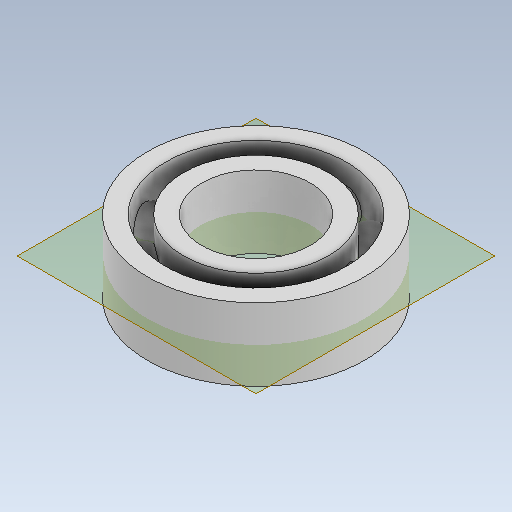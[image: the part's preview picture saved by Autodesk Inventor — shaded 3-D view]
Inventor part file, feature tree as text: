
AUTODESK INVENTOR PART (.ipt)
format: ipt  version: 2020 (Build 240168000, 168)  size: 228,864 bytes
history: native  units: mm
features: sketch x3, extrude x2, plane x1, revolve x1, pattern_circular x1, projected_geometry x1
ambient origin geometry x8: Origin, YZ Plane, XZ Plane, XY Plane, X Axis, Y Axis, Z Axis, Center Point
bodies: Solid1 (feature_tree)
feature tree (9):
  extrude  "Extrusion1"  Depth=3.0mm
  extrude  "Extrusion2"  Depth=4.0mm
  plane  "Work Plane1"
  revolve  "Revolution1"  [1 undecoded]
  pattern_circular  "Circular Pattern1"  [2 undecoded]
  sketch  "Sketch1"  dims[d0=6.0mm d1=3.0mm]
  sketch  "Sketch2"  dims[d2=2.0mm d3=0.0mm d4=4.0mm]
  projected_geometry  "Projected Loop1"
  sketch  "Sketch3"  dims[d5=5.0mm d6=2.0mm d7=0.0mm d8=1.0mm d9=90.0deg d10=100.0mm d11=360.0deg]
note: 3 required parameter values undecoded (feature->parameter linkage not recoverable at this tier; creation-order binding heuristic only, values carry confidence <= 0.55)